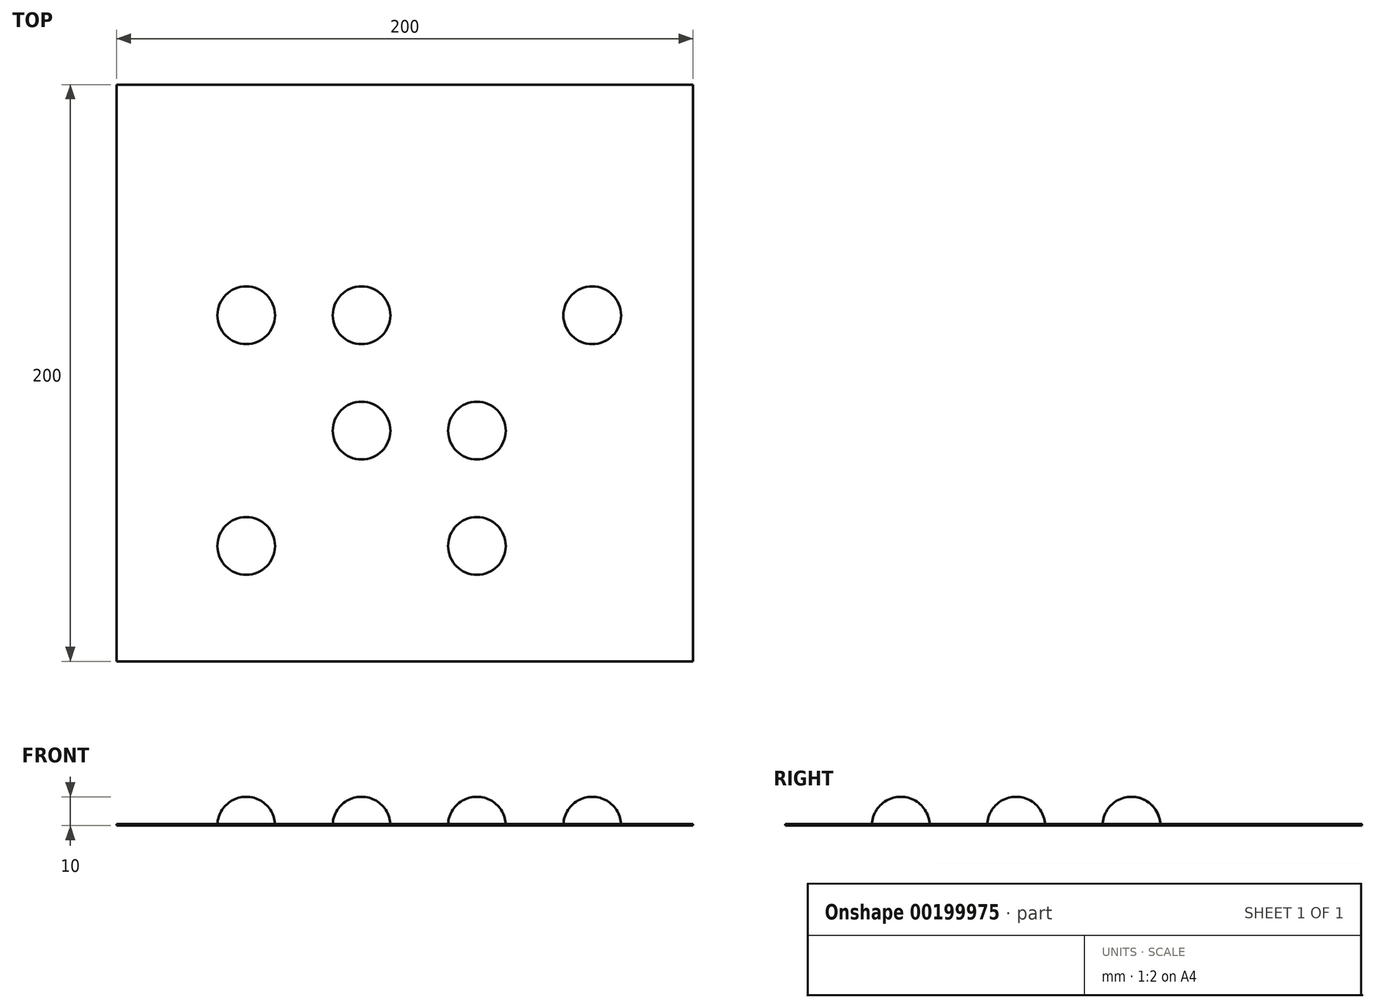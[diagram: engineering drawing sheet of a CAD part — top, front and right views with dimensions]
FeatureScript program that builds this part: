
annotation { "Feature Type Name" : "Feature", "Feature Type Description" : "" }
export const myFeature = defineFeature(function(context is Context, id is Id, definition is map)
    precondition{}
    {
        {
            var Q0;
            Q0=qCreatedBy(makeId("Top.planeOp"),FACE);
            var sketch = newSketch(context, id + "F0", { "sketchPlane" : qUnion([Q0])});
            skLineSegment(sketch, "E0.bottom", {"start": v(-100, 100) * mm, "end": v(100, 100) * mm});
            skLineSegment(sketch, "E0.top", {"start": v(-100, -100) * mm, "end": v(100, -100) * mm});
            skLineSegment(sketch, "E0.left", {"start": v(-100, 100) * mm, "end": v(-100, -100) * mm});
            skLineSegment(sketch, "E0.right", {"start": v(100, 100) * mm, "end": v(100, -100) * mm});
            skPoint(sketch, "E0.middle", {"position": v(0, 0) * mm});
            skSolve(sketch);
        }
        {
            var Q0;
            Q0=makeQuery(id+"F0.imprint","IMPRINT",FACE,{"disambiguationData":[TD([[makeQuery(id+"F0.imprint","IMPRINT",EDGE,{"derivedFrom":sQuery(id+"F0.wireOp",EDGE,"E0.bottom")}),-1.0]])]});
            var sketch = newSketch(context, id + "F1", { "sketchPlane" : qUnion([Q0])});
            skCircle(sketch, "E1", {"center": v(-55, -60) * mm, "radius": 10 * mm});
            skCircle(sketch, "E2.0.2.0", {"center": v(-55, 20) * mm, "radius": 10 * mm});
            skCircle(sketch, "E2.1.1.0", {"center": v(-15, -20) * mm, "radius": 10 * mm});
            skCircle(sketch, "E2.1.2.0", {"center": v(-15, 20) * mm, "radius": 10 * mm});
            skCircle(sketch, "E2.2.0.0", {"center": v(25, -60) * mm, "radius": 10 * mm});
            skCircle(sketch, "E2.2.1.0", {"center": v(25, -20) * mm, "radius": 10 * mm});
            skCircle(sketch, "E2.3.2.0", {"center": v(65, 20) * mm, "radius": 10 * mm});
            skLineSegment(sketch, "E2.direction1", {"start": v(-55, -60) * mm, "end": v(-15, -60) * mm, "construction": true});
            skLineSegment(sketch, "E2.direction2", {"start": v(-55, -60) * mm, "end": v(-55, -20) * mm, "construction": true});
            skSolve(sketch);
        }
        {
            var Q0;
            Q0=makeQuery(id+"F1.imprint","IMPRINT",FACE,{"disambiguationData":[TD([[makeQuery(id+"F1.imprint","IMPRINT",EDGE,{"derivedFrom":sQuery(id+"F1.wireOp",EDGE,"E1")}),-1.0]])]});
            extrude(context, id + "F2", {"entities" : qUnion([Q0]), "depth" : 0.5 * mm});
        }
        {
            var Q0;
            Q0 = qSketchRegion(id + "F1", true);
            extrude(context, id + "F3", {"entities" : qUnion([Q0]), "operationType" : NewBodyOperationType.ADD, "depth" : 10 * mm});
        }
        {
            var Q0;
            Q0=makeQuery(id+"F3.opExtrude","CAP_EDGE",EDGE,{"disambiguationData":[OSD([sQuery(id+"F1.wireOp",EDGE,"E2.0.2.0")])],"isStart":false});
            var Q1;
            Q1=makeQuery(id+"F3.opExtrude","CAP_EDGE",EDGE,{"disambiguationData":[OSD([sQuery(id+"F1.wireOp",EDGE,"E2.1.2.0")])],"isStart":false});
            var Q2;
            Q2=makeQuery(id+"F3.opExtrude","CAP_EDGE",EDGE,{"disambiguationData":[OSD([sQuery(id+"F1.wireOp",EDGE,"E2.3.2.0")])],"isStart":false});
            var Q3;
            Q3=makeQuery(id+"F3.opExtrude","CAP_EDGE",EDGE,{"disambiguationData":[OSD([sQuery(id+"F1.wireOp",EDGE,"E2.2.1.0")])],"isStart":false});
            var Q4;
            Q4=makeQuery(id+"F3.opExtrude","CAP_EDGE",EDGE,{"disambiguationData":[OSD([sQuery(id+"F1.wireOp",EDGE,"E2.1.1.0")])],"isStart":false});
            var Q5;
            Q5=makeQuery(id+"F3.opExtrude","CAP_EDGE",EDGE,{"disambiguationData":[OSD([sQuery(id+"F1.wireOp",EDGE,"E1")])],"isStart":false});
            var Q6;
            Q6=makeQuery(id+"F3.opExtrude","CAP_EDGE",EDGE,{"disambiguationData":[OSD([sQuery(id+"F1.wireOp",EDGE,"E2.2.0.0")])],"isStart":false});
            fillet(context, id + "F4", {"entities" : qUnion([Q0, Q1, Q2, Q3, Q4, Q5, Q6]), "radius" : 10 * mm, "tangentPropagation" : true, "allowEdgeOverflow" : false});
        }
    });
